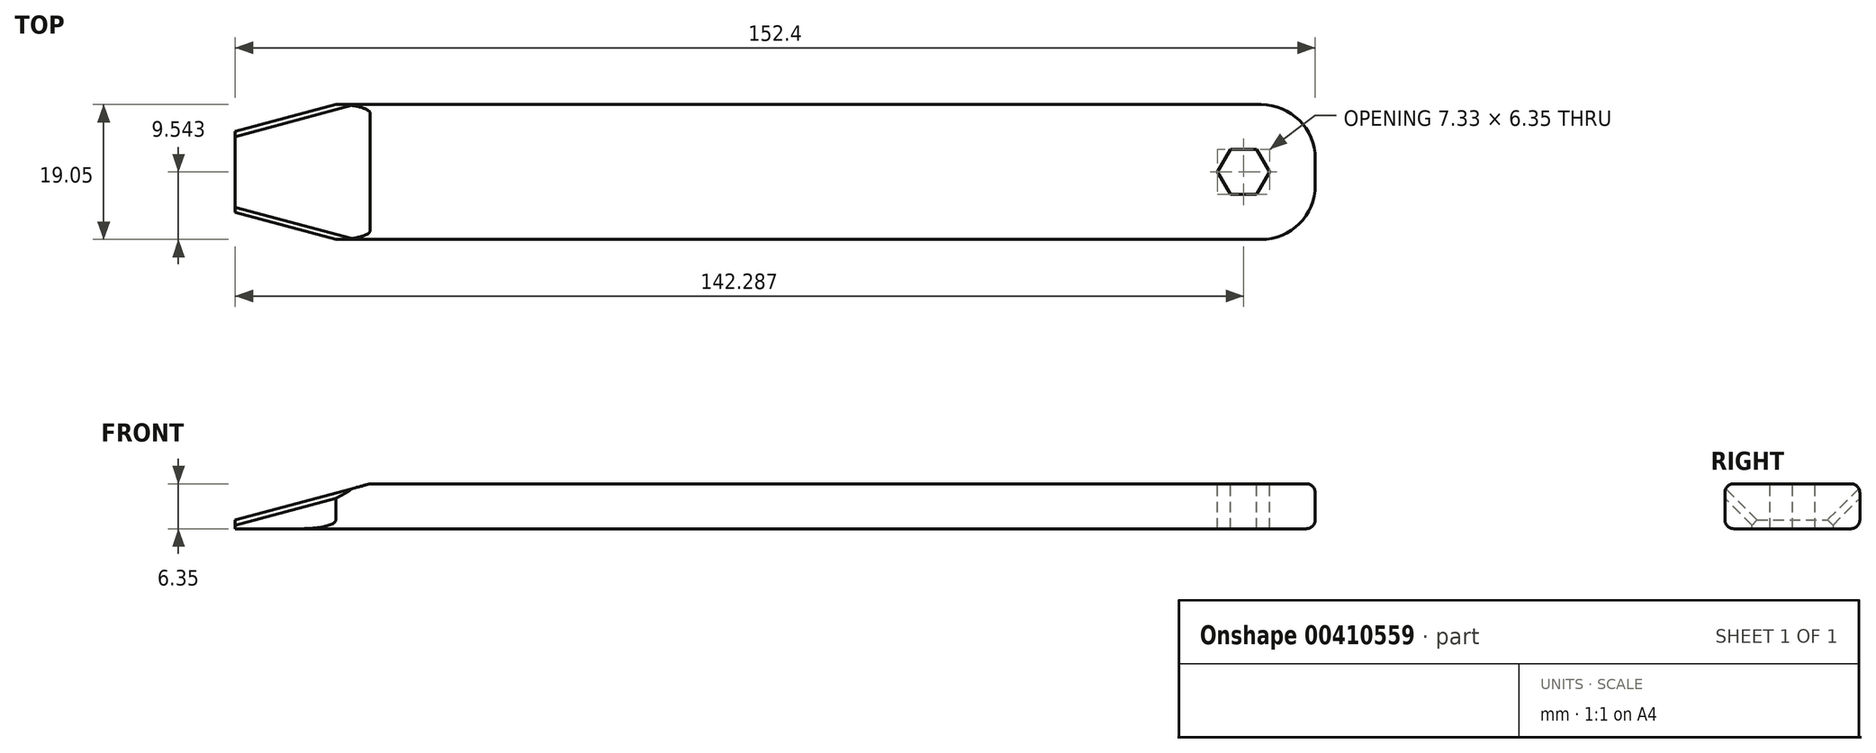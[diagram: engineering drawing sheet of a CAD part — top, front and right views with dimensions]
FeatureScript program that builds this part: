
annotation { "Feature Type Name" : "Feature", "Feature Type Description" : "" }
export const myFeature = defineFeature(function(context is Context, id is Id, definition is map)
    precondition{}
    {
        {
            var Q0;
            Q0=qCreatedBy(makeId("Top.planeOp"),FACE);
            var sketch = newSketch(context, id + "F0", { "sketchPlane" : qUnion([Q0])});
            skLineSegment(sketch, "E0.bottom", {"start": v(-43.2, -23.69) * mm, "end": v(-31.83, -23.69) * mm});
            skLineSegment(sketch, "E0.top", {"start": v(-43.2, -27.13) * mm, "end": v(-31.83, -27.13) * mm});
            skLineSegment(sketch, "E0.left", {"start": v(-43.2, -23.69) * mm, "end": v(-43.2, -27.13) * mm});
            skLineSegment(sketch, "E0.right", {"start": v(-31.83, -23.69) * mm, "end": v(-31.83, -27.13) * mm});
            skSolve(sketch);
        }
        {
            var Q0;
            Q0=makeQuery(id+"F0.imprint","IMPRINT",FACE,{"disambiguationData":[TD([[makeQuery(id+"F0.imprint","IMPRINT",EDGE,{"derivedFrom":sQuery(id+"F0.wireOp",EDGE,"E0.bottom")}),-1.0]])]});
            extrude(context, id + "F1", {"entities" : qUnion([Q0]), "depth" : 6.35 * mm});
        }
        {
            var Q0;
            Q0=makeQuery(id+"F1.opExtrude","SWEPT_FACE",FACE,{"disambiguationData":[OSD([sQuery(id+"F0.wireOp",EDGE,"E0.top")])]});
            extrude(context, id + "F2", {"entities" : qUnion([Q0]), "operationType" : NewBodyOperationType.ADD, "depth" : 15.6 * mm});
        }
        {
            var Q0;
            {var subQ0=sQuery(id+"F0.wireOp",EDGE,"E0.right");Q0=makeQuery(id+"F2.boolean.opBoolean","MERGE",FACE,{"derivedFrom":[makeQuery(id+"F1.opExtrude","SWEPT_FACE",FACE,{"disambiguationData":[OSD([subQ0])]}),makeQuery(id+"F2.opExtrude","SWEPT_FACE",FACE,{"disambiguationData":[OSD([sQuery(id+"F0.wireOp",EDGE,"E0.top"),subQ0])]})]});}
            extrude(context, id + "F3", {"entities" : qUnion([Q0]), "operationType" : NewBodyOperationType.ADD, "depth" : 141.04 * mm});
        }
        {
            var Q0;
            {var subQ0=sQuery(id+"F0.wireOp",EDGE,"E0.right");var subQ1=sQuery(id+"F0.wireOp",EDGE,"E0.top");Q0=makeQuery(id+"F3.opExtrude","CAP_EDGE",EDGE,{"disambiguationData":[OSD([subQ1,subQ0]),TDD([makeQuery(id+"F2.opExtrude","CAP_EDGE",EDGE,{"disambiguationData":[OSD([subQ1,subQ0])],"isStart":false})])],"isStart":false});}
            fillet(context, id + "F4", {"entities" : qUnion([Q0]), "radius" : 7.62 * mm, "tangentPropagation" : true, "allowEdgeOverflow" : false});
        }
        {
            var Q0;
            Q0=makeQuery(id+"F3.opExtrude","CAP_EDGE",EDGE,{"disambiguationData":[OSD([sQuery(id+"F0.wireOp",EDGE,"E0.bottom"),sQuery(id+"F0.wireOp",EDGE,"E0.right")])],"isStart":false});
            fillet(context, id + "F5", {"entities" : qUnion([Q0]), "radius" : 7.62 * mm, "tangentPropagation" : true, "allowEdgeOverflow" : false});
        }
        {
            var Q0;
            {var subQ0=sQuery(id+"F0.wireOp",EDGE,"E0.left");var subQ1=sQuery(id+"F0.wireOp",EDGE,"E0.top");Q0=makeQuery(id+"F2.boolean.opBoolean","MERGE",EDGE,{"derivedFrom":[makeQuery(id+"F1.opExtrude","CAP_EDGE",EDGE,{"disambiguationData":[OSD([subQ0])],"isStart":false}),makeQuery(id+"F2.opExtrude","SWEPT_EDGE",EDGE,{"disambiguationData":[OSD([subQ1,subQ0]),TDD([makeQuery(id+"F1.opExtrude","CAP_VERTEX",VERTEX,{"disambiguationData":[OSD([subQ1,subQ0])],"isStart":false})])]})]});}
            chamfer(context, id + "F6", {"entities" : qUnion([Q0]), "chamferType" : ChamferType.OFFSET_ANGLE, "width" : 19.05 * mm, "oppositeDirection" : false, "angle" : 15 * degree, "tangentPropagation" : true});
        }
        {
            var Q0;
            Q0=makeQuery(id+"F1.opExtrude","SWEPT_EDGE",EDGE,{"disambiguationData":[OSD([sQuery(id+"F0.wireOp",EDGE,"E0.bottom"),sQuery(id+"F0.wireOp",EDGE,"E0.left")])]});
            chamfer(context, id + "F7", {"entities" : qUnion([Q0]), "chamferType" : ChamferType.OFFSET_ANGLE, "width" : 3.8 * mm, "oppositeDirection" : false, "angle" : 75 * degree, "tangentPropagation" : true});
        }
        {
            var Q0;
            Q0=makeQuery(id+"F2.opExtrude","CAP_EDGE",EDGE,{"disambiguationData":[OSD([sQuery(id+"F0.wireOp",EDGE,"E0.top"),sQuery(id+"F0.wireOp",EDGE,"E0.left")])],"isStart":false});
            chamfer(context, id + "F8", {"entities" : qUnion([Q0]), "chamferType" : ChamferType.OFFSET_ANGLE, "width" : 3.8 * mm, "oppositeDirection" : true, "angle" : 75 * degree, "tangentPropagation" : true});
        }
        {
            var Q0;
            {var subQ0=sQuery(id+"F0.wireOp",EDGE,"E0.right");var subQ1=sQuery(id+"F0.wireOp",EDGE,"E0.top");Q0=makeQuery(id+"F3.boolean.opBoolean","MERGE",EDGE,{"derivedFrom":[makeQuery(id+"F2.opExtrude","CAP_EDGE",EDGE,{"disambiguationData":[OSD([subQ1]),TDD([makeQuery(id+"F1.opExtrude","CAP_EDGE",EDGE,{"disambiguationData":[OSD([subQ1])],"isStart":false})])],"isStart":false}),makeQuery(id+"F3.opExtrude","SWEPT_EDGE",EDGE,{"disambiguationData":[OSD([subQ1,subQ0]),TDD([makeQuery(id+"F2.opExtrude","CAP_VERTEX",VERTEX,{"disambiguationData":[OSD([subQ1,subQ0]),TDD([makeQuery(id+"F1.opExtrude","CAP_VERTEX",VERTEX,{"disambiguationData":[OSD([subQ1,subQ0])],"isStart":false})])],"isStart":false})])]})]});}
            fillet(context, id + "F9", {"entities" : qUnion([Q0]), "radius" : 1.27 * mm, "tangentPropagation" : true, "allowEdgeOverflow" : false});
        }
        {
            var Q0;
            {var subQ0=sQuery(id+"F0.wireOp",EDGE,"E0.right");var subQ1=sQuery(id+"F0.wireOp",EDGE,"E0.top");Q0=makeQuery(id+"F3.boolean.opBoolean","MERGE",EDGE,{"derivedFrom":[makeQuery(id+"F2.opExtrude","CAP_EDGE",EDGE,{"disambiguationData":[OSD([subQ1]),TDD([makeQuery(id+"F1.opExtrude","CAP_EDGE",EDGE,{"disambiguationData":[OSD([subQ1])],"isStart":true})])],"isStart":false}),makeQuery(id+"F3.opExtrude","SWEPT_EDGE",EDGE,{"disambiguationData":[OSD([subQ1,subQ0]),TDD([makeQuery(id+"F2.opExtrude","CAP_VERTEX",VERTEX,{"disambiguationData":[OSD([subQ1,subQ0]),TDD([makeQuery(id+"F1.opExtrude","CAP_VERTEX",VERTEX,{"disambiguationData":[OSD([subQ1,subQ0])],"isStart":true})])],"isStart":false})])]})]});}
            fillet(context, id + "F10", {"entities" : qUnion([Q0]), "radius" : 1.27 * mm, "tangentPropagation" : true, "allowEdgeOverflow" : false});
        }
        {
            var Q0;
            {var subQ0=sQuery(id+"F0.wireOp",EDGE,"E0.right");var subQ1=sQuery(id+"F0.wireOp",EDGE,"E0.top");Q0=makeQuery(id+"F3.boolean.opBoolean","MERGE",FACE,{"derivedFrom":[makeQuery(id+"F2.boolean.opBoolean","MERGE",FACE,{"derivedFrom":[makeQuery(id+"F1.opExtrude","CAP_FACE",FACE,{"disambiguationData":[OSD([sQuery(id+"F0.wireOp",EDGE,"E0.bottom"),subQ1,sQuery(id+"F0.wireOp",EDGE,"E0.left"),subQ0])],"isStart":false}),makeQuery(id+"F2.opExtrude","SWEPT_FACE",FACE,{"disambiguationData":[OSD([subQ1]),TDD([makeQuery(id+"F1.opExtrude","CAP_EDGE",EDGE,{"disambiguationData":[OSD([subQ1])],"isStart":false})])]})]}),makeQuery(id+"F3.opExtrude","SWEPT_FACE",FACE,{"disambiguationData":[OSD([subQ1,subQ0]),TDD([makeQuery(id+"F2.boolean.opBoolean","MERGE",EDGE,{"derivedFrom":[makeQuery(id+"F1.opExtrude","CAP_EDGE",EDGE,{"disambiguationData":[OSD([subQ0])],"isStart":false}),makeQuery(id+"F2.opExtrude","SWEPT_EDGE",EDGE,{"disambiguationData":[OSD([subQ1,subQ0]),TDD([makeQuery(id+"F1.opExtrude","CAP_VERTEX",VERTEX,{"disambiguationData":[OSD([subQ1,subQ0])],"isStart":false})])]})]})])]})]});}
            var sketch = newSketch(context, id + "F11", { "sketchPlane" : qUnion([Q0])});
            skLineSegment(sketch, "E1", {"start": v(99.1, -42.74) * mm, "end": v(99.1, -33.2) * mm});
            skSolve(sketch);
        }
        {
            var Q0;
            {var subQ0=sQuery(id+"F0.wireOp",EDGE,"E0.right");var subQ1=sQuery(id+"F0.wireOp",EDGE,"E0.top");var subQ2=makeQuery(id+"F1.opExtrude","CAP_VERTEX",VERTEX,{"disambiguationData":[OSD([subQ1,subQ0])],"isStart":false});var subQ3=makeQuery(id+"F2.boolean.opBoolean","MERGE",EDGE,{"derivedFrom":[makeQuery(id+"F1.opExtrude","CAP_EDGE",EDGE,{"disambiguationData":[OSD([subQ0])],"isStart":false}),makeQuery(id+"F2.opExtrude","SWEPT_EDGE",EDGE,{"disambiguationData":[OSD([subQ1,subQ0]),TDD([subQ2])]})]});var subQ4=makeQuery(id+"F1.opExtrude","CAP_EDGE",EDGE,{"disambiguationData":[OSD([subQ1])],"isStart":false});var subQ5=sQuery(id+"F0.wireOp",EDGE,"E0.left");var subQ6=sQuery(id+"F0.wireOp",EDGE,"E0.bottom");var subQ7=makeQuery(id+"F3.boolean.opBoolean","MERGE",FACE,{"derivedFrom":[makeQuery(id+"F2.boolean.opBoolean","MERGE",FACE,{"derivedFrom":[makeQuery(id+"F1.opExtrude","CAP_FACE",FACE,{"disambiguationData":[OSD([subQ6,subQ1,subQ5,subQ0])],"isStart":false}),makeQuery(id+"F2.opExtrude","SWEPT_FACE",FACE,{"disambiguationData":[OSD([subQ1]),TDD([subQ4])]})]}),makeQuery(id+"F3.opExtrude","SWEPT_FACE",FACE,{"disambiguationData":[OSD([subQ1,subQ0]),TDD([subQ3])]})]});var subQ8=subQ7;var subQ9=subQ8;var subQ10=subQ9;Q0=makeQuery(id+"F11.imprint","IMPRINT",FACE,{"disambiguationData":[TD([[makeQuery(id+"F11.imprint","IMPRINT",EDGE,{"derivedFrom":makeQuery(id+"F9.opFillet","BLEND_EDGE",EDGE,{"blendedFrom":[makeQuery(id+"F3.opExtrude","CAP_EDGE",EDGE,{"disambiguationData":[OSD([subQ1,subQ0]),TDD([subQ3])],"isStart":false}),subQ10],"blendedInto":[subQ10]})}),1.0]])]});}
            var sketch = newSketch(context, id + "F12", { "sketchPlane" : qUnion([Q0])});
            skLineSegment(sketch, "E2", {"start": v(99.1, -33.2) * mm, "end": v(99.1, -36.37) * mm});
            skCircle(sketch, "E3.cCircle", {"center": v(99.1, -33.2) * mm, "radius": 3.18 * mm, "construction": true});
            skLineSegment(sketch, "E3.0", {"start": v(100.93, -36.37) * mm, "end": v(97.26, -36.37) * mm});
            skLineSegment(sketch, "E3.1", {"start": v(97.26, -36.37) * mm, "end": v(95.43, -33.2) * mm});
            skLineSegment(sketch, "E3.2", {"start": v(95.43, -33.2) * mm, "end": v(97.26, -30.02) * mm});
            skLineSegment(sketch, "E3.3", {"start": v(97.26, -30.02) * mm, "end": v(100.93, -30.02) * mm});
            skLineSegment(sketch, "E3.4", {"start": v(100.93, -30.02) * mm, "end": v(102.76, -33.2) * mm});
            skLineSegment(sketch, "E3.5", {"start": v(102.76, -33.2) * mm, "end": v(100.93, -36.37) * mm});
            skPoint(sketch, "E3.0.midPoint", {"position": v(99.1, -36.37) * mm});
            skSolve(sketch);
        }
        {
            var Q0;
            Q0 = qSketchRegion(id + "F12", true);
            extrude(context, id + "F13", {"entities" : qUnion([Q0]), "operationType" : NewBodyOperationType.REMOVE, "oppositeDirection" : true, "depth" : 25.4 * mm});
        }
        {
            var Q0;
            {var subQ0=sQuery(id+"F0.wireOp",EDGE,"E0.left");var subQ1=sQuery(id+"F0.wireOp",EDGE,"E0.top");Q0=makeQuery(id+"F8.opChamfer","BLEND_EDGE",EDGE,{"blendedFrom":[makeQuery(id+"F2.opExtrude","CAP_EDGE",EDGE,{"disambiguationData":[OSD([subQ1,subQ0])],"isStart":false}),makeQuery(id+"F6.opChamfer","BLEND_FACE",FACE,{"disambiguationData":[OSD([subQ1,subQ0])]})],"blendedInto":[makeQuery(id+"F6.opChamfer","BLEND_FACE",FACE,{"disambiguationData":[OSD([subQ1,subQ0])]})]});}
            chamfer(context, id + "F14", {"entities" : qUnion([Q0]), "width" : 0.76 * mm, "tangentPropagation" : true});
        }
        {
            var Q0;
            {var subQ0=sQuery(id+"F0.wireOp",EDGE,"E0.left");Q0=makeQuery(id+"F7.opChamfer","BLEND_EDGE",EDGE,{"blendedFrom":[makeQuery(id+"F1.opExtrude","SWEPT_EDGE",EDGE,{"disambiguationData":[OSD([sQuery(id+"F0.wireOp",EDGE,"E0.bottom"),subQ0])]}),makeQuery(id+"F6.opChamfer","BLEND_FACE",FACE,{"disambiguationData":[OSD([sQuery(id+"F0.wireOp",EDGE,"E0.top"),subQ0])]})],"blendedInto":[makeQuery(id+"F6.opChamfer","BLEND_FACE",FACE,{"disambiguationData":[OSD([sQuery(id+"F0.wireOp",EDGE,"E0.top"),subQ0])]})]});}
            chamfer(context, id + "F15", {"entities" : qUnion([Q0]), "width" : 0.76 * mm, "tangentPropagation" : true});
        }
    });
